# Revit family: RN 90023 Optifitt-Serra-Verlängerung reduziert
name_source: partatom
category: Rohrformteile
units: mm (PartAtom-declared; Revit-internal decimal feet)

## family parameters
Arbeitsebenenbasiert = Nein
Beim Laden mit Abzugskörper schneiden = Nein
Bemaßung runder Anschluss = Durchmesser verwenden
Gemeinsam genutzt = Nein
Immer vertikal = Ja
Teiletyp = Nicht definiert

## types (7) — shared parameters
1.010.00.2 Blattnummer der Richtlinie = 29
1.010.00.3 Ausgabedatum (Monat) der Richtlinie = 201308
1.010.00.4 Herstellername = R. Nussbaum AG
1.010.00.5 Revisionsdatum der Datei = 20190521
1.010.00.6 Webadresse des Herstellers = http://www.nussbaum.ch
1.100.00.4 Produktbezeichnung = Versorgung
1.110.00.2 Index = 3
1.110.00.4 Produktbezeichnung = Optifitt-Serra
1.960/3L.00.8 Link (URL) = https://www.nussbaum.ch
29.700.00.4 Produktname = Optifitt-Serra-Verlängerung reduziert
29.700.00.5 Produktkennung = 2
29.700.00.6 Querschnittsform = 1
29.700.00.7 Nennweitensystem = DN
29.700.00.8 Nenndrucksystem = PN
29.710.02.4 Nenndruck = 16
29.710.02.5 max. zul. Überdruck [hPa] = 1600
29.710.02.7 max. zul. Dauer-Betriebsdruck [hPa] = 1600
29.710.02.9 max. zul. Dauer-Betriebstemperatur [°C] = 90
Connector Visibility = Nein
EnclosingSpace Visibility = Nein
Hersteller = R. Nussbaum AG
URL = https://www.nussbaum.ch

## per-type parameters (varying)
| type | 1.800.00.3 TGA-Nummer | 1.800.00.4 Kommentarfeld | 1.810.00.3 Hersteller-Bestellnummer | 1.810.00.4 DATANORM-Nummer | 1.810.00.6 GTIN-Nummer | 29.710.02.10 Formstück-Gewicht [kg] | 29.710.02.3 Benennung | CONNECTOR0_DIAMETER_dX_0r | CONNECTOR0_dX_01 | CONNECTOR0_ref_dX | CONNECTOR1_DIAMETER_dX_0r | CONNECTOR1_dX_00 | CONNECTOR1_dX_01 | CONNECTOR1_ref_dX | Modell | R. Nussbaum AG 90023.21 de Visibility | R. Nussbaum AG 90023.23 de Visibility | R. Nussbaum AG 90023.25 de Visibility | R. Nussbaum AG 90023.26 de Visibility | R. Nussbaum AG 90023.28 de Visibility | R. Nussbaum AG 90023.29 de Visibility | R. Nussbaum AG 90023.32 de Visibility | Typenkommentare |
| DN=32x25 | 01900300000000000000000000000000000000000000000013000000000000000007 | 90023.32, Optifitt-Serra-Verlängerung reduziert, DN=32x25, L=48, R=1, Rp=1¼ | 90023.32 | 90023.32 | 7612945033406 | 0.18 | Optifitt-Serra-Verlängerung reduziert, DN=32x25, L=48, R=1, Rp=1¼ | 25 mm | 17 mm | 17 mm | 25 mm | 31 mm | 48 mm | 48 mm | 90023.32 | Nein | Nein | Nein | Nein | Nein | Nein | Ja | Optifitt-Serra-Verlängerung reduziert DN=32x25 |
| DN=25x20 | 01900300000000000000000000000000000000000000000013000000000000000006 | 90023.29, Optifitt-Serra-Verlängerung reduziert, DN=25x20, L=42, R=¾, Rp=1 | 90023.29 | 90023.29 | 7612945033390 | 0.141 | Optifitt-Serra-Verlängerung reduziert, DN=25x20, L=42, R=¾, Rp=1 | 25 mm | 17 mm | 17 mm | 20 mm | 27 mm | 42 mm  [stored 0.137795 ft] | 42 mm  [stored 0.137795 ft] | 90023.29 | Nein | Nein | Nein | Nein | Nein | Ja | Nein | Optifitt-Serra-Verlängerung reduziert DN=25x20 |
| DN=25x15 | 01900300000000000000000000000000000000000000000013000000000000000005 | 90023.28, Optifitt-Serra-Verlängerung reduziert, DN=25x15, L=39, R=½, Rp=1 | 90023.28 | 90023.28 | 7612945033383 | 0.12 | Optifitt-Serra-Verlängerung reduziert, DN=25x15, L=39, R=½, Rp=1 | 25 mm | 17 mm | 17 mm | 15 mm | 26 mm | 39 mm | 39 mm | 90023.28 | Nein | Nein | Nein | Nein | Ja | Nein | Nein | Optifitt-Serra-Verlängerung reduziert DN=25x15 |
| DN=20x15 | 01900300000000000000000000000000000000000000000013000000000000000004 | 90023.26, Optifitt-Serra-Verlängerung reduziert, DN=20x15, L=37, R=½, Rp=¾ | 90023.26 | 90023.26 | 7612945033376 | 0.094 | Optifitt-Serra-Verlängerung reduziert, DN=20x15, L=37, R=½, Rp=¾ | 20 mm | 15 mm | 15 mm | 15 mm | 24 mm  [stored 0.0787402 ft] | 37 mm | 37 mm | 90023.26 | Nein | Nein | Nein | Ja | Nein | Nein | Nein | Optifitt-Serra-Verlängerung reduziert DN=20x15 |
| DN=20x12 | 01900300000000000000000000000000000000000000000013000000000000000003 | 90023.25, Optifitt-Serra-Verlängerung reduziert, DN=20x12, L=35, R=3/8, Rp=¾ | 90023.25 | 90023.25 | 7612945033369 | 0.091 | Optifitt-Serra-Verlängerung reduziert, DN=20x12, L=35, R=3/8, Rp=¾ | 20 mm | 15 mm | 15 mm | 10 mm  [stored 0.0328084 ft] | 25 mm | 35 mm | 35 mm | 90023.25 | Nein | Nein | Ja | Nein | Nein | Nein | Nein | Optifitt-Serra-Verlängerung reduziert DN=20x12 |
| DN=15x12 | 01900300000000000000000000000000000000000000000013000000000000000002 | 90023.23, Optifitt-Serra-Verlängerung reduziert, DN=15x12, L=32, R=3/8, Rp=½ | 90023.23 | 90023.23 | 7612945033352 | 0.057 | Optifitt-Serra-Verlängerung reduziert, DN=15x12, L=32, R=3/8, Rp=½ | 15 mm | 13 mm | 13 mm | 10 mm  [stored 0.0328084 ft] | 22 mm | 32 mm | 32 mm | 90023.23 | Nein | Ja | Nein | Nein | Nein | Nein | Nein | Optifitt-Serra-Verlängerung reduziert DN=15x12 |
| DN=12x10 | 01900300000000000000000000000000000000000000000013000000000000000001 | 90023.21, Optifitt-Serra-Verlängerung reduziert, DN=12x10, L=27, R=¼, Rp=3/8 | 90023.21 | 90023.21 | 7612945033345 | 0.032 | Optifitt-Serra-Verlängerung reduziert, DN=12x10, L=27, R=¼, Rp=3/8 | 10 mm  [stored 0.0328084 ft] | 10 mm  [stored 0.0328084 ft] | 10 mm  [stored 0.0328084 ft] | 8 mm  [stored 0.0262467 ft] | 17 mm | 27 mm | 27 mm | 90023.21 | Ja | Nein | Nein | Nein | Nein | Nein | Nein | Optifitt-Serra-Verlängerung reduziert DN=12x10 |

note: [stored X ft] marks values corroborated as IEEE doubles in the binary element streams (Revit-internal decimal feet)

## geometry (parser evidence)
native form markers: Sweep x1
no freeform markers — native parametric forms only
